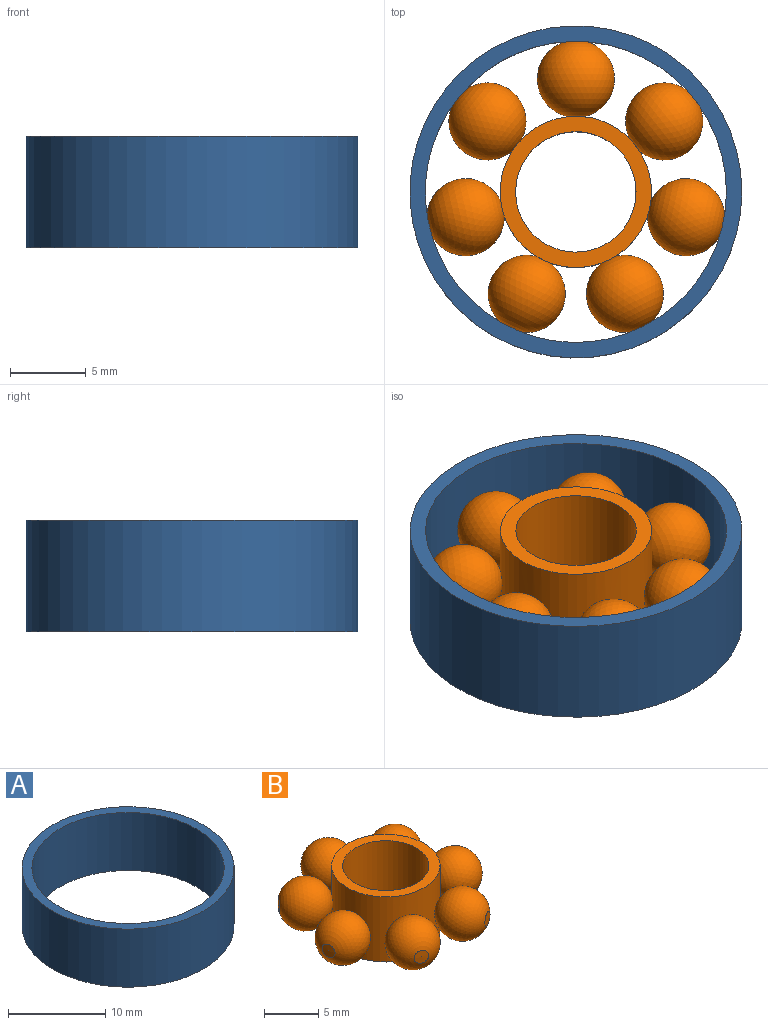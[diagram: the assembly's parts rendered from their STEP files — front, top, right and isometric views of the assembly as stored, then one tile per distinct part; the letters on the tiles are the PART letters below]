
ASSEMBLY  parts=2 mates=1
PART A: 4 faces, bbox 21.8x21.8x7.3 mm
  f0: cylinder r=9.91mm len=19.81mm, axis (0,0,-1), area 455.3mm2, adj f2,f3
  f1: cylinder r=10.92mm len=21.84mm, axis (0,0,-1), area 502mm2, adj f2,f3
  f2: plane 21.84x21.84mm, normal (0,0,1), area 66.5mm2, adj f0,f1
  f3: plane 21.84x21.84mm, normal (0,0,-1), area 66.5mm2, adj f0,f1
PART B: 18 faces, bbox 19.6x19.2x7.3 mm
  f0: cylinder r=4.98mm len=9.96mm, axis (0,0,-1), area 222mm2, adj f2,f3,f4,f6,f8,f10,f12,f14
  f1: cylinder r=3.96mm len=7.92mm, axis (0,0,-1), area 182.1mm2, adj f2,f3
  f2: plane 9.96x9.96mm, normal (0,0,1), area 28.5mm2, adj f0,f1
  f3: plane 9.96x9.96mm, normal (0,0,-1), area 28.5mm2, adj f0,f1
  f4: sphere r=2.54mm, area 78.5mm2, adj f0,f5
  f5: sphere r=9.91mm, area 1.6mm2, adj f4
  f6: sphere r=2.54mm, area 78.5mm2, adj f0,f7
  f7: sphere r=9.91mm, area 1.6mm2, adj f6
  f8: sphere r=2.54mm, area 78.5mm2, adj f0,f9
  f9: sphere r=9.91mm, area 1.6mm2, adj f8
  f10: sphere r=2.54mm, area 78.5mm2, adj f0,f11
  f11: sphere r=9.91mm, area 1.6mm2, adj f10
  f12: sphere r=2.54mm, area 78.5mm2, adj f0,f13
  f13: sphere r=9.91mm, area 1.6mm2, adj f12
  f14: sphere r=2.54mm, area 78.5mm2, adj f0,f15
  f15: sphere r=9.91mm, area 1.6mm2, adj f14
  f16: sphere r=2.54mm, area 78.5mm2, adj f0,f17
  f17: sphere r=9.91mm, area 1.6mm2, adj f16
PLACE A t=(-2.62,-2.92,-2.11)mm
PLACE B t=(-2.62,-2.92,-2.11)mm
MATE fastened A.f0 <-> B.f0  axis (0,0,-1) through (-2.62,-2.92,-2.11)mm
